# Revit family: XLP_SUPPLY
name_source: partatom
category: Mechanical Equipment
units: mm (PartAtom-declared; Revit-internal decimal feet)

## family parameters
Always vertical = Yes
Cut with Voids When Loaded = No
Part Type = Normal
Room Calculation Point = No
Round Connector Dimension = Use Diameter
Shared = No
Work Plane-Based = No

## types (8) — shared parameters
0 = 0' - 0"
1" = 0' - 1"
1.5 = 0' - 1 1/2"
1/2 = 0' - 0 1/2"
135 = 135.00°
2" = 0' - 2"
2' = 2' - 0"
3" = 0' - 3"
4" = 0' - 4"
4'6" = 4' - 6"
45 = 45.00°
9" = 0' - 9"
90 = 90.00°
Manufacturer = Loren Cook Company
Model = XLP-Supply
ONE EIGTH = 0' - 0 1/8"
Type Comments = Low Pressure Wall-Pac Supply Fan Steel Propeller Belt Drive
URL = www.lorencook.com

## per-type parameters (varying)
- 24_XLP_SUPPLY: (A/2)-1"=1' - 2 27/32"; (A/2)-C-.5"=0' - 7 27/32"; (D_SUP/2)-(C/2)-.125"=0' - 11 1/2"; (SIZE/2)-.25"=1' - 2 11/16"; -((A/2)-C-.5")=-0' - 7 27/32"; -((SIZE/2)-.25")=-1' - 2 11/16"; -B=-1' - 7 1/16"; -B+1"=-1' - 5 1/16"; -C/2=-0' - 3 3/8"; -D=-0' - 3"; -D_PAC/2=-1' - 8 3/16"; -WH_B/2=-1' - 5"; 2E=0' - 6"; A=2' - 6 3/16"; A/2=1' - 3 3/32"; A/3.5=0' - 8 5/8"; A/7=0' - 4 5/16"; A_PAC=2' - 9 1/2"; A_PAC/2=1' - 4 3/4"; B=1' - 7 1/16"; B-2.5"=1' - 4 9/16"; B/2=0' - 9 17/32"; B/4=0' - 4 25/32"; B_PAC=2' - 7"; B_PAC/2=1' - 3 1/2"; C=0' - 6 3/4"; C/2=0' - 3 3/8"; C_PAC=2' - 3 1/2"; C_PAC/2=1' - 1 3/4"; D=2' - 6"; D/2=1' - 3"; D_PAC=2' - 10 3/8"; D_PAC/2=1' - 2 3/16"; E=0' - 3"; E/2=0' - 1 1/2"; MOTOR=0' - 3 3/4"; SIZE=2' - 5 7/8"; SIZE/2=1' - 2 15/16"; WH_A=2' - 3 1/8"; WH_B=2' - 10"; WH_B/2=1' - 5"; WH_C=3' - 1"; WO_PAC=2' - 7 1/4"; WO_PAC/2=1' - 3 5/8"
- 30_XLP_SUPPLY: (A/2)-1"=1' - 5 27/32"; (A/2)-C-.5"=0' - 10 27/32"; (D_SUP/2)-(C/2)-.125"=1' - 2 1/2"; (SIZE/2)-.25"=1' - 5 11/16"; -((A/2)-C-.5")=-0' - 10 27/32"; -((SIZE/2)-.25")=-1' - 5 11/16"; -B=-1' - 7 1/16"; -B+1"=-1' - 5 1/16"; -C/2=-0' - 3 3/8"; -D=-0' - 3"; -D_PAC/2=-1' - 10"; -WH_B/2=-1' - 8"; 2E=0' - 6"; A=3' - 0 3/16"; A/2=1' - 6 3/32"; A/3.5=0' - 10 11/32"; A/7=0' - 5 5/32"; A_PAC=3' - 3 1/2"; A_PAC/2=1' - 7 3/4"; B=1' - 7 1/16"; B-2.5"=1' - 4 9/16"; B/2=0' - 9 17/32"; B/4=0' - 4 25/32"; B_PAC=3' - 1"; B_PAC/2=1' - 6 1/2"; C=0' - 6 3/4"; C/2=0' - 3 3/8"; C_PAC=2' - 9 1/2"; C_PAC/2=1' - 4 3/4"; D=3' - 0"; D/2=1' - 6"; D_PAC=3' - 2"; D_PAC/2=1' - 4"; E=0' - 3"; E/2=0' - 1 1/2"; MOTOR=0' - 4 1/2"; SIZE=2' - 11 7/8"; SIZE/2=1' - 5 15/16"; WH_A=2' - 7 7/16"; WH_B=3' - 4"; WH_B/2=1' - 8"; WH_C=3' - 7"; WO_PAC=3' - 1 1/4"; WO_PAC/2=1' - 6 5/8"
- 36_XLP_SUPPLY: (A/2)-1"=1' - 8 27/32"; (A/2)-C-.5"=1' - 1 7/32"; (D_SUP/2)-(C/2)-.125"=1' - 5 3/16"; (SIZE/2)-.25"=1' - 8 11/16"; -((A/2)-C-.5")=-1' - 1 7/32"; -((SIZE/2)-.25")=-1' - 8 11/16"; -B=-1' - 7 1/16"; -B+1"=-1' - 5 1/16"; -C/2=-0' - 3 11/16"; -D=-0' - 3"; -D_PAC/2=-1' - 10 3/4"; -WH_B/2=-1' - 11"; 2E=0' - 6"; A=3' - 6 3/16"; A/2=1' - 9 3/32"; A/3.5=1' - 0 1/16"; A/7=0' - 6 1/32"; A_PAC=3' - 9 1/2"; A_PAC/2=1' - 10 3/4"; B=1' - 7 1/16"; B-2.5"=1' - 4 9/16"; B/2=0' - 9 17/32"; B/4=0' - 4 25/32"; B_PAC=3' - 7"; B_PAC/2=1' - 9 1/2"; C=0' - 7 3/8"; C/2=0' - 3 11/16"; C_PAC=3' - 3 1/2"; C_PAC/2=1' - 7 3/4"; D=3' - 6"; D/2=1' - 9"; D_PAC=3' - 3 1/2"; D_PAC/2=1' - 4 3/4"; E=0' - 3"; E/2=0' - 1 1/2"; MOTOR=0' - 5 1/4"; SIZE=3' - 5 7/8"; SIZE/2=1' - 8 15/16"; WH_A=2' - 11 11/16"; WH_B=3' - 10"; WH_B/2=1' - 11"; WH_C=4' - 1"; WO_PAC=3' - 7 1/4"; WO_PAC/2=1' - 9 5/8"
- 42_XLP_SUPPLY: (A/2)-1"=1' - 11 27/32"; (A/2)-C-.5"=1' - 4 1/32"; (D_SUP/2)-(C/2)-.125"=1' - 8 3/32"; (SIZE/2)-.25"=1' - 11 11/16"; -((A/2)-C-.5")=-1' - 4 1/32"; -((SIZE/2)-.25")=-1' - 11 11/16"; -B=-1' - 8 11/16"; -B+1"=-1' - 6 11/16"; -C/2=-0' - 3 25/32"; -D=-0' - 3"; -D_PAC/2=-1' - 11 1/2"; -WH_B/2=-2' - 2"; 2E=0' - 6"; A=4' - 0 3/16"; A/2=2' - 0 3/32"; A/3.5=1' - 1 25/32"; A/7=0' - 6 7/8"; A_PAC=4' - 3 1/2"; A_PAC/2=2' - 1 3/4"; B=1' - 8 11/16"; B-2.5"=1' - 6 3/16"; B/2=0' - 10 11/32"; B/4=0' - 5 3/16"; B_PAC=4' - 1 1/16"; B_PAC/2=2' - 0 17/32"; C=0' - 7 9/16"; C/2=0' - 3 25/32"; C_PAC=3' - 9 1/2"; C_PAC/2=1' - 10 3/4"; D=4' - 0"; D/2=2' - 0"; D_PAC=3' - 5"; D_PAC/2=1' - 5 1/2"; E=0' - 3"; E/2=0' - 1 1/2"; MOTOR=0' - 6"; SIZE=3' - 11 7/8"; SIZE/2=1' - 11 15/16"; WH_A=3' - 3 15/16"; WH_B=4' - 4"; WH_B/2=2' - 2"; WH_C=4' - 7"; WO_PAC=4' - 1 5/16"; WO_PAC/2=2' - 0 21/32"
- 48_XLP_SUPPLY: (A/2)-1"=2' - 2 27/32"; (A/2)-C-.5"=1' - 6 23/32"; (D_SUP/2)-(C/2)-.125"=1' - 10 15/16"; (SIZE/2)-.25"=2' - 2 11/16"; -((A/2)-C-.5")=-1' - 6 23/32"; -((SIZE/2)-.25")=-2' - 2 11/16"; -B=-2' - 2 5/16"; -B+1"=-2' - 0 5/16"; -C/2=-0' - 3 15/16"; -D=-0' - 3"; -D_PAC/2=-2' - 4 1/2"; -WH_B/2=-2' - 5"; 2E=0' - 6"; A=4' - 6 3/16"; A/2=2' - 3 3/32"; A/3.5=1' - 3 15/32"; A/7=0' - 7 3/4"; A_PAC=4' - 9 1/2"; A_PAC/2=2' - 4 3/4"; B=2' - 2 5/16"; B-2.5"=1' - 11 13/16"; B/2=1' - 1 5/32"; B/4=0' - 6 19/32"; B_PAC=4' - 7 1/16"; B_PAC/2=2' - 3 17/32"; C=0' - 7 7/8"; C/2=0' - 3 15/16"; C_PAC=4' - 3 1/2"; C_PAC/2=2' - 1 3/4"; D=4' - 6"; D/2=2' - 3"; D_PAC=4' - 3"; D_PAC/2=1' - 10 1/2"; E=0' - 3"; E/2=0' - 1 1/2"; MOTOR=0' - 6 3/4"; SIZE=4' - 5 7/8"; SIZE/2=2' - 2 15/16"; WH_A=3' - 8 3/16"; WH_B=4' - 10"; WH_B/2=2' - 5"; WH_C=5' - 1"; WO_PAC=4' - 7 5/16"; WO_PAC/2=2' - 3 21/32"
- 54_XLP_SUPPLY: (A/2)-1"=2' - 5 27/32"; (A/2)-C-.5"=1' - 9 27/32"; (D_SUP/2)-(C/2)-.125"=2' - 2"; (SIZE/2)-.25"=2' - 5 11/16"; -((A/2)-C-.5")=-1' - 9 27/32"; -((SIZE/2)-.25")=-2' - 5 11/16"; -B=-2' - 2 5/16"; -B+1"=-2' - 0 5/16"; -C/2=-0' - 3 7/8"; -D=-0' - 3"; -D_PAC/2=-2' - 3"; -WH_B/2=-2' - 8"; 2E=0' - 6"; A=5' - 0 3/16"; A/2=2' - 6 3/32"; A/3.5=1' - 5 3/16"; A/7=0' - 8 19/32"; A_PAC=5' - 3 1/2"; A_PAC/2=2' - 7 3/4"; B=2' - 2 5/16"; B-2.5"=1' - 11 13/16"; B/2=1' - 1 5/32"; B/4=0' - 6 19/32"; B_PAC=5' - 1 1/8"; B_PAC/2=2' - 6 9/16"; C=0' - 7 3/4"; C/2=0' - 3 7/8"; C_PAC=4' - 9 1/2"; C_PAC/2=2' - 4 3/4"; D=5' - 0"; D/2=2' - 6"; D_PAC=4' - 0"; D_PAC/2=1' - 9"; E=0' - 3"; E/2=0' - 1 1/2"; MOTOR=0' - 7 1/2"; SIZE=4' - 11 7/8"; SIZE/2=2' - 5 15/16"; WH_A=4' - 0 7/16"; WH_B=5' - 4"; WH_B/2=2' - 8"; WH_C=5' - 7"; WO_PAC=5' - 1 3/8"; WO_PAC/2=2' - 6 11/16"
- 60_XLP_SUPPLY: (A/2)-1"=2' - 8 27/32"; (A/2)-C-.5"=2' - 0 23/32"; (D_SUP/2)-(C/2)-.125"=2' - 4 15/16"; (SIZE/2)-.25"=2' - 8 11/16"; -((A/2)-C-.5")=-2' - 0 23/32"; -((SIZE/2)-.25")=-2' - 8 11/16"; -B=-2' - 2 5/16"; -B+1"=-2' - 0 5/16"; -C/2=-0' - 3 15/16"; -D=-0' - 3"; -D_PAC/2=-2' - 3"; -WH_B/2=-2' - 11"; 2E=0' - 6"; A=5' - 6 3/16"; A/2=2' - 9 3/32"; A/3.5=1' - 6 29/32"; A/7=0' - 9 15/32"; A_PAC=5' - 9 1/2"; A_PAC/2=2' - 10 3/4"; B=2' - 2 5/16"; B-2.5"=1' - 11 13/16"; B/2=1' - 1 5/32"; B/4=0' - 6 19/32"; B_PAC=5' - 7 1/8"; B_PAC/2=2' - 9 9/16"; C=0' - 7 7/8"; C/2=0' - 3 15/16"; C_PAC=5' - 3 1/2"; C_PAC/2=2' - 7 3/4"; D=5' - 6"; D/2=2' - 9"; D_PAC=4' - 0"; D_PAC/2=1' - 9"; E=0' - 3"; E/2=0' - 1 1/2"; MOTOR=0' - 8 1/4"; SIZE=5' - 5 7/8"; SIZE/2=2' - 8 15/16"; WH_A=4' - 4 5/8"; WH_B=5' - 10"; WH_B/2=2' - 11"; WH_C=6' - 1"; WO_PAC=5' - 7 3/8"; WO_PAC/2=2' - 9 11/16"
- 20_XLP_SUPPLY: (A/2)-1"=0' - 11 27/32"; (A/2)-C-.5"=0' - 6 11/32"; (D_SUP/2)-(C/2)-.125"=0' - 9 1/4"; (SIZE/2)-.25"=0' - 11 11/16"; -((A/2)-C-.5")=-0' - 6 11/32"; -((SIZE/2)-.25")=-0' - 11 11/16"; -B=-1' - 7 1/16"; -B+1"=-1' - 5 1/16"; -C/2=-0' - 2 5/8"; -D=-0' - 2"; -D_PAC/2=-1' - 8 3/16"; -WH_B/2=-1' - 3"; 2E=0' - 4"; A=2' - 0 3/16"; A/2=1' - 0 3/32"; A/3.5=0' - 6 29/32"; A/7=0' - 3 15/32"; A_PAC=2' - 3 1/2"; A_PAC/2=1' - 1 3/4"; B=1' - 7 1/16"; B-2.5"=1' - 4 9/16"; B/2=0' - 9 17/32"; B/4=0' - 4 25/32"; B_PAC=2' - 1"; B_PAC/2=1' - 0 1/2"; C=0' - 5 1/4"; C/2=0' - 2 5/8"; C_PAC=1' - 10"; C_PAC/2=0' - 11"; D=2' - 0"; D/2=1' - 0"; D_PAC=2' - 10 3/8"; D_PAC/2=1' - 2 3/16"; E=0' - 2"; E/2=0' - 1"; MOTOR=0' - 3"; SIZE=1' - 11 7/8"; SIZE/2=0' - 11 15/16"; WH_A=2' - 0 3/8"; WH_B=2' - 6"; WH_B/2=1' - 3"; WH_C=2' - 9"; WO_PAC=2' - 1 1/4"; WO_PAC/2=1' - 0 5/8"

## geometry (parser evidence)
native form markers: Sweep x3
no freeform markers — native parametric forms only
